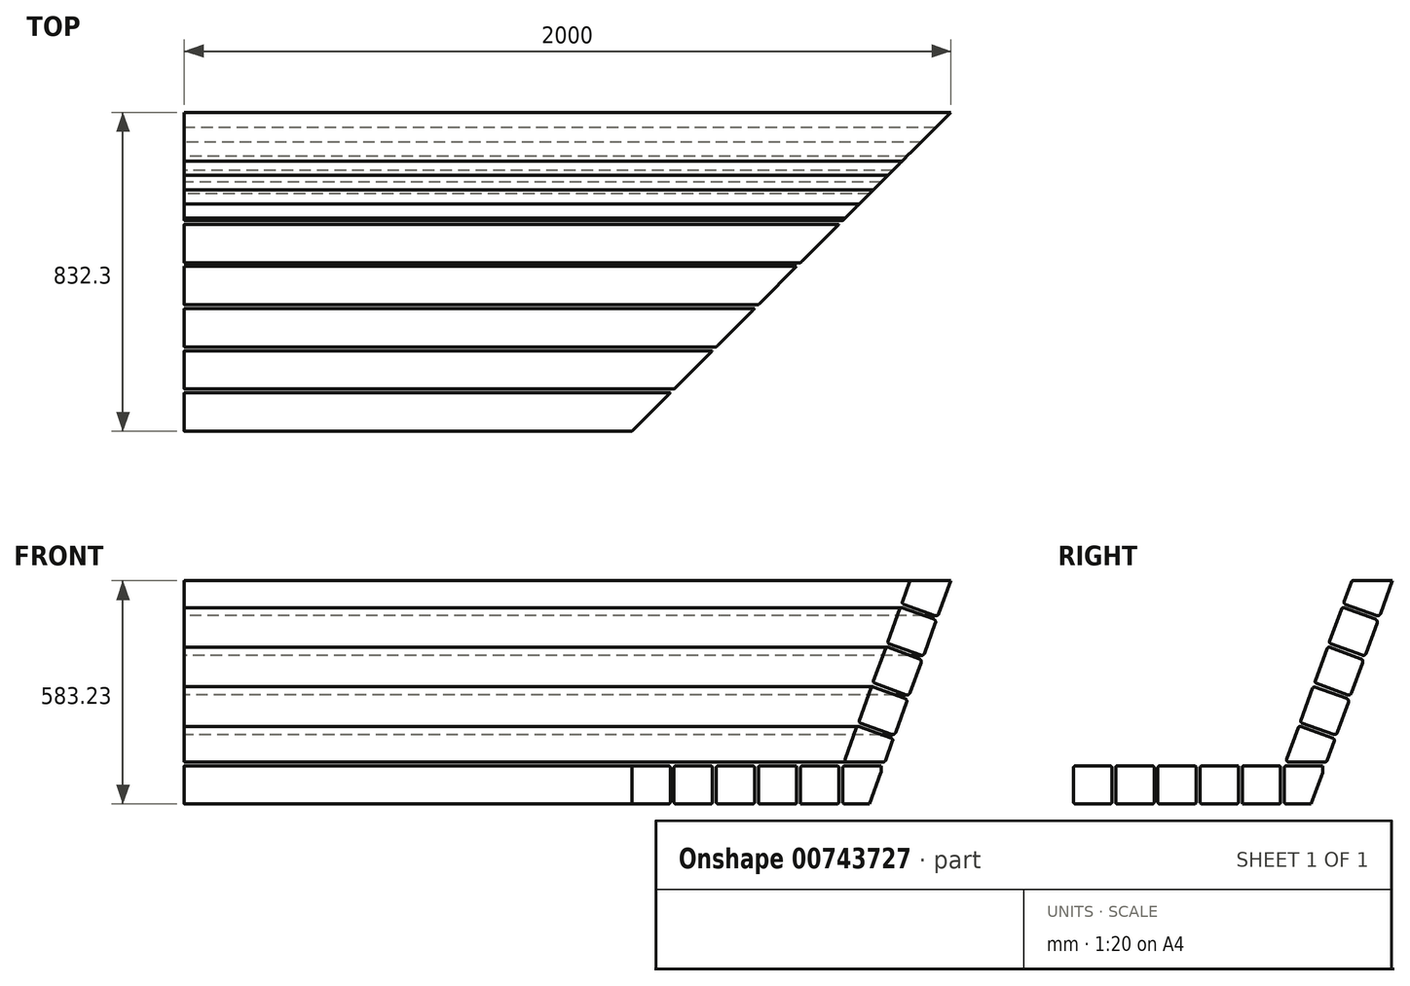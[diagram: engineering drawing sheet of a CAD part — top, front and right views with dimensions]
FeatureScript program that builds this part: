
annotation { "Feature Type Name" : "Feature", "Feature Type Description" : "" }
export const myFeature = defineFeature(function(context is Context, id is Id, definition is map)
    precondition{}
    {
        {
            var Q0;
            Q0=qCreatedBy(makeId("Right.planeOp"),FACE);
            var sketch = newSketch(context, id + "F0", { "sketchPlane" : qUnion([Q0])});
            skLineSegment(sketch, "E0.bottom", {"start": v(0, 0) * mm, "end": v(-95, 0) * mm});
            skLineSegment(sketch, "E0.top", {"start": v(-33.48, -100) * mm, "end": v(-95, -100) * mm});
            skLineSegment(sketch, "E0.left", {"start": v(0, 0) * mm, "end": v(0, -16.75) * mm});
            skLineSegment(sketch, "E0.right", {"start": v(-100, -5) * mm, "end": v(-100, -95) * mm});
            skLineSegment(sketch, "E1.1.0.0", {"start": v(-115, 0) * mm, "end": v(-205, 0) * mm});
            skLineSegment(sketch, "E1.1.0.1", {"start": v(-210, -5) * mm, "end": v(-210, -100) * mm});
            skLineSegment(sketch, "E1.1.0.2", {"start": v(-115, -100) * mm, "end": v(-210, -100) * mm});
            skLineSegment(sketch, "E1.1.0.3", {"start": v(-110, -5) * mm, "end": v(-110, -95) * mm});
            skLineSegment(sketch, "E1.2.0.0", {"start": v(-220, 0) * mm, "end": v(-315, 0) * mm});
            skLineSegment(sketch, "E1.2.0.1", {"start": v(-320, -5) * mm, "end": v(-320, -95) * mm});
            skLineSegment(sketch, "E1.2.0.2", {"start": v(-225, -100) * mm, "end": v(-315, -100) * mm});
            skLineSegment(sketch, "E1.2.0.3", {"start": v(-220, 0) * mm, "end": v(-220, -95) * mm});
            skLineSegment(sketch, "E1.3.0.0", {"start": v(-335, 0) * mm, "end": v(-425, 0) * mm});
            skLineSegment(sketch, "E1.3.0.1", {"start": v(-430, -5) * mm, "end": v(-430, -95) * mm});
            skLineSegment(sketch, "E1.3.0.2", {"start": v(-335, -100) * mm, "end": v(-425, -100) * mm});
            skLineSegment(sketch, "E1.3.0.3", {"start": v(-330, -5) * mm, "end": v(-330, -95) * mm});
            skLineSegment(sketch, "E1.4.0.0", {"start": v(-445, 0) * mm, "end": v(-535, 0) * mm});
            skLineSegment(sketch, "E1.4.0.1", {"start": v(-540, -5) * mm, "end": v(-540, -95) * mm});
            skLineSegment(sketch, "E1.4.0.2", {"start": v(-445, -100) * mm, "end": v(-535, -100) * mm});
            skLineSegment(sketch, "E1.4.0.3", {"start": v(-440, -5) * mm, "end": v(-440, -95) * mm});
            skLineSegment(sketch, "E1.5.0.0", {"start": v(-555, 0) * mm, "end": v(-645, 0) * mm});
            skLineSegment(sketch, "E1.5.0.1", {"start": v(-650, -5) * mm, "end": v(-650, -95) * mm});
            skLineSegment(sketch, "E1.5.0.2", {"start": v(-555, -100) * mm, "end": v(-645, -100) * mm});
            skLineSegment(sketch, "E1.5.0.3", {"start": v(-550, -5) * mm, "end": v(-550, -95) * mm});
            skLineSegment(sketch, "E1.direction1", {"start": v(-100, 0) * mm, "end": v(-210, 0) * mm, "construction": true});
            skLineSegment(sketch, "E2", {"start": v(-93.92, 16.71) * mm, "end": v(-63.87, 99.27) * mm});
            skLineSegment(sketch, "E3", {"start": v(-89.22, 10) * mm, "end": v(6.56, 10) * mm});
            skLineSegment(sketch, "E4", {"start": v(-57.46, 102.26) * mm, "end": v(27.11, 71.48) * mm});
            skLineSegment(sketch, "E5", {"start": v(30.1, 65.07) * mm, "end": v(11.25, 13.29) * mm});
            skPoint(sketch, "E6.orphan", {"position": v(0, -17.63) * mm});
            skLineSegment(sketch, "E7", {"start": v(-54.04, 111.66) * mm, "end": v(27.7, 81.9) * mm});
            skLineSegment(sketch, "E8", {"start": v(37.98, 86.7) * mm, "end": v(66.69, 165.6) * mm});
            skLineSegment(sketch, "E9", {"start": v(61.9, 175.88) * mm, "end": v(-19.84, 205.63) * mm});
            skLineSegment(sketch, "E10.trimOffspring", {"start": v(-57.03, 118.06) * mm, "end": v(-26.25, 202.64) * mm});
            skLineSegment(sketch, "E11", {"start": v(-19.4, 221.43) * mm, "end": v(11.38, 306) * mm});
            skLineSegment(sketch, "E12", {"start": v(182.3, 483.23) * mm, "end": v(150.84, 396.8) * mm});
            skLineSegment(sketch, "E13", {"start": v(-16.42, 215.02) * mm, "end": v(65.31, 185.27) * mm});
            skLineSegment(sketch, "E14", {"start": v(17.78, 309) * mm, "end": v(99.52, 279.24) * mm});
            skLineSegment(sketch, "E15", {"start": v(21.2, 318.39) * mm, "end": v(102.94, 288.64) * mm});
            skLineSegment(sketch, "E16", {"start": v(55.4, 412.36) * mm, "end": v(137.14, 382.6) * mm});
            skLineSegment(sketch, "E17", {"start": v(58.83, 421.75) * mm, "end": v(140.56, 392) * mm});
            skLineSegment(sketch, "E18", {"start": v(182.3, 483.23) * mm, "end": v(79.38, 483.23) * mm});
            skLineSegment(sketch, "E19.trimOffspring", {"start": v(141.93, 372.33) * mm, "end": v(113.22, 293.44) * mm});
            skLineSegment(sketch, "E20.trimOffspring", {"start": v(55.84, 428.16) * mm, "end": v(74.68, 479.94) * mm});
            skLineSegment(sketch, "E21.trimOffspring", {"start": v(18.22, 324.8) * mm, "end": v(49, 409.37) * mm});
            skLineSegment(sketch, "E22.trimOffspring", {"start": v(104.31, 268.96) * mm, "end": v(75.6, 190.07) * mm});
            skLineSegment(sketch, "E23", {"start": v(-0.3, -18.46) * mm, "end": v(-28.78, -96.71) * mm});
            skPoint(sketch, "E24.orphan", {"position": v(0, -100) * mm});
            skArc(sketch, "E25.filletArc", {"start": v(-650, -95) * mm, "mid": v(-648.54, -98.54) * mm, "end": v(-645, -100) * mm});
            skPoint(sketch, "E26.visualSharp", {"position": v(-550, -100) * mm});
            skArc(sketch, "E26.filletArc", {"start": v(-555, -100) * mm, "mid": v(-551.46, -98.54) * mm, "end": v(-550, -95) * mm});
            skPoint(sketch, "E27.visualSharp", {"position": v(-550, 0) * mm});
            skArc(sketch, "E27.filletArc", {"start": v(-550, -5) * mm, "mid": v(-551.46, -1.46) * mm, "end": v(-555, 0) * mm});
            skArc(sketch, "E28.filletArc", {"start": v(-645, 0) * mm, "mid": v(-648.54, -1.46) * mm, "end": v(-650, -5) * mm});
            skPoint(sketch, "E29.visualSharp", {"position": v(-540, 0) * mm});
            skArc(sketch, "E29.filletArc", {"start": v(-535, 0) * mm, "mid": v(-538.54, -1.46) * mm, "end": v(-540, -5) * mm});
            skPoint(sketch, "E30.visualSharp", {"position": v(-540, -100) * mm});
            skArc(sketch, "E30.filletArc", {"start": v(-540, -95) * mm, "mid": v(-538.54, -98.54) * mm, "end": v(-535, -100) * mm});
            skPoint(sketch, "E31.visualSharp", {"position": v(-440, 0) * mm});
            skArc(sketch, "E31.filletArc", {"start": v(-440, -5) * mm, "mid": v(-441.46, -1.46) * mm, "end": v(-445, 0) * mm});
            skPoint(sketch, "E32.visualSharp", {"position": v(-430, 0) * mm});
            skArc(sketch, "E32.filletArc", {"start": v(-425, 0) * mm, "mid": v(-428.54, -1.46) * mm, "end": v(-430, -5) * mm});
            skPoint(sketch, "E33.visualSharp", {"position": v(-440, -100) * mm});
            skArc(sketch, "E33.filletArc", {"start": v(-445, -100) * mm, "mid": v(-441.46, -98.54) * mm, "end": v(-440, -95) * mm});
            skPoint(sketch, "E34.visualSharp", {"position": v(-430, -100) * mm});
            skArc(sketch, "E34.filletArc", {"start": v(-430, -95) * mm, "mid": v(-428.54, -98.54) * mm, "end": v(-425, -100) * mm});
            skPoint(sketch, "E35.visualSharp", {"position": v(-330, 0) * mm});
            skArc(sketch, "E35.filletArc", {"start": v(-330, -5) * mm, "mid": v(-331.46, -1.46) * mm, "end": v(-335, 0) * mm});
            skPoint(sketch, "E36.visualSharp", {"position": v(-330, -100) * mm});
            skArc(sketch, "E36.filletArc", {"start": v(-335, -100) * mm, "mid": v(-331.46, -98.54) * mm, "end": v(-330, -95) * mm});
            skPoint(sketch, "E37.visualSharp", {"position": v(-320, 0) * mm});
            skArc(sketch, "E37.filletArc", {"start": v(-315, 0) * mm, "mid": v(-318.54, -1.46) * mm, "end": v(-320, -5) * mm});
            skPoint(sketch, "E38.visualSharp", {"position": v(-320, -100) * mm});
            skArc(sketch, "E38.filletArc", {"start": v(-320, -95) * mm, "mid": v(-318.54, -98.54) * mm, "end": v(-315, -100) * mm});
            skPoint(sketch, "E39.visualSharp", {"position": v(-220, -100) * mm});
            skArc(sketch, "E39.filletArc", {"start": v(-225, -100) * mm, "mid": v(-221.46, -98.54) * mm, "end": v(-220, -95) * mm});
            skPoint(sketch, "E40.visualSharp", {"position": v(-210, 0) * mm});
            skArc(sketch, "E40.filletArc", {"start": v(-205, 0) * mm, "mid": v(-208.54, -1.46) * mm, "end": v(-210, -5) * mm});
            skPoint(sketch, "E41.visualSharp", {"position": v(-110, -100) * mm});
            skArc(sketch, "E41.filletArc", {"start": v(-115, -100) * mm, "mid": v(-111.46, -98.54) * mm, "end": v(-110, -95) * mm});
            skPoint(sketch, "E42.visualSharp", {"position": v(-110, 0) * mm});
            skArc(sketch, "E42.filletArc", {"start": v(-110, -5) * mm, "mid": v(-111.46, -1.46) * mm, "end": v(-115, 0) * mm});
            skPoint(sketch, "E43.visualSharp", {"position": v(-100, -100) * mm});
            skArc(sketch, "E43.filletArc", {"start": v(-100, -95) * mm, "mid": v(-98.54, -98.54) * mm, "end": v(-95, -100) * mm});
            skPoint(sketch, "E44.visualSharp", {"position": v(-29.98, -100) * mm});
            skPoint(sketch, "E45.visualSharp", {"position": v(-100, 0) * mm});
            skArc(sketch, "E45.filletArc", {"start": v(-95, 0) * mm, "mid": v(-98.54, -1.46) * mm, "end": v(-100, -5) * mm});
            skArc(sketch, "E46.filletArc", {"start": v(-0.3, -18.46) * mm, "mid": v(-0.08, -17.62) * mm, "end": v(0, -16.75) * mm});
            skPoint(sketch, "E47.visualSharp", {"position": v(-96.36, 10) * mm});
            skArc(sketch, "E47.filletArc", {"start": v(-93.92, 16.71) * mm, "mid": v(-93.32, 12.13) * mm, "end": v(-89.22, 10) * mm});
            skPoint(sketch, "E48.visualSharp", {"position": v(10.06, 10) * mm});
            skArc(sketch, "E48.filletArc", {"start": v(6.56, 10) * mm, "mid": v(9.42, 10.9) * mm, "end": v(11.25, 13.29) * mm});
            skPoint(sketch, "E49.visualSharp", {"position": v(-62.16, 103.97) * mm});
            skArc(sketch, "E49.filletArc", {"start": v(-57.46, 102.26) * mm, "mid": v(-61.28, 102.1) * mm, "end": v(-63.87, 99.27) * mm});
            skPoint(sketch, "E50.visualSharp", {"position": v(35.23, 79.16) * mm});
            skArc(sketch, "E50.filletArc", {"start": v(27.7, 81.9) * mm, "mid": v(33.83, 82.18) * mm, "end": v(37.98, 86.7) * mm});
            skPoint(sketch, "E51.visualSharp", {"position": v(-58.74, 113.37) * mm});
            skArc(sketch, "E51.filletArc", {"start": v(-57.03, 118.06) * mm, "mid": v(-56.86, 114.24) * mm, "end": v(-54.04, 111.66) * mm});
            skPoint(sketch, "E52.visualSharp", {"position": v(31.81, 69.77) * mm});
            skArc(sketch, "E52.filletArc", {"start": v(30.1, 65.07) * mm, "mid": v(29.93, 68.9) * mm, "end": v(27.11, 71.48) * mm});
            skPoint(sketch, "E53.visualSharp", {"position": v(69.43, 173.13) * mm});
            skArc(sketch, "E53.filletArc", {"start": v(66.69, 165.6) * mm, "mid": v(66.42, 171.73) * mm, "end": v(61.9, 175.88) * mm});
            skPoint(sketch, "E54.visualSharp", {"position": v(-21.12, 216.73) * mm});
            skArc(sketch, "E54.filletArc", {"start": v(-19.4, 221.43) * mm, "mid": v(-19.24, 217.6) * mm, "end": v(-16.42, 215.02) * mm});
            skPoint(sketch, "E55.visualSharp", {"position": v(-24.54, 207.34) * mm});
            skArc(sketch, "E55.filletArc", {"start": v(-19.84, 205.63) * mm, "mid": v(-23.66, 205.46) * mm, "end": v(-26.25, 202.64) * mm});
            skPoint(sketch, "E56.visualSharp", {"position": v(72.85, 182.53) * mm});
            skArc(sketch, "E56.filletArc", {"start": v(65.31, 185.27) * mm, "mid": v(71.45, 185.54) * mm, "end": v(75.6, 190.07) * mm});
            skPoint(sketch, "E57.visualSharp", {"position": v(107.06, 276.5) * mm});
            skArc(sketch, "E57.filletArc", {"start": v(104.31, 268.96) * mm, "mid": v(104.04, 275.1) * mm, "end": v(99.52, 279.24) * mm});
            skPoint(sketch, "E58.visualSharp", {"position": v(110.48, 285.9) * mm});
            skArc(sketch, "E58.filletArc", {"start": v(102.94, 288.64) * mm, "mid": v(109.07, 288.9) * mm, "end": v(113.22, 293.44) * mm});
            skPoint(sketch, "E59.visualSharp", {"position": v(16.5, 320.1) * mm});
            skArc(sketch, "E59.filletArc", {"start": v(18.22, 324.8) * mm, "mid": v(18.38, 320.97) * mm, "end": v(21.2, 318.39) * mm});
            skPoint(sketch, "E60.visualSharp", {"position": v(13.09, 310.7) * mm});
            skArc(sketch, "E60.filletArc", {"start": v(17.78, 309) * mm, "mid": v(13.96, 308.82) * mm, "end": v(11.38, 306) * mm});
            skPoint(sketch, "E61.visualSharp", {"position": v(144.68, 379.87) * mm});
            skArc(sketch, "E61.filletArc", {"start": v(141.93, 372.33) * mm, "mid": v(141.67, 378.46) * mm, "end": v(137.14, 382.6) * mm});
            skPoint(sketch, "E62.visualSharp", {"position": v(54.13, 423.46) * mm});
            skArc(sketch, "E62.filletArc", {"start": v(55.84, 428.16) * mm, "mid": v(56, 424.34) * mm, "end": v(58.83, 421.75) * mm});
            skPoint(sketch, "E63.visualSharp", {"position": v(182.3, 483.23) * mm});
            skPoint(sketch, "E64.visualSharp", {"position": v(148.1, 389.26) * mm});
            skArc(sketch, "E64.filletArc", {"start": v(140.56, 392) * mm, "mid": v(146.7, 392.27) * mm, "end": v(150.84, 396.8) * mm});
            skPoint(sketch, "E65.visualSharp", {"position": v(50.7, 414.07) * mm});
            skArc(sketch, "E65.filletArc", {"start": v(55.4, 412.36) * mm, "mid": v(51.58, 412.2) * mm, "end": v(49, 409.37) * mm});
            skPoint(sketch, "E66.visualSharp", {"position": v(75.88, 483.23) * mm});
            skArc(sketch, "E66.filletArc", {"start": v(79.38, 483.23) * mm, "mid": v(76.52, 482.33) * mm, "end": v(74.68, 479.94) * mm});
            skLineSegment(sketch, "E67", {"start": v(-28.78, -96.71) * mm, "end": v(-29.98, -100) * mm});
            skLineSegment(sketch, "E68", {"start": v(-29.98, -100) * mm, "end": v(-33.48, -100) * mm});
            skLineSegment(sketch, "E69", {"start": v(-29.38, -98.36) * mm, "end": v(-29.98, -100) * mm});
            skSolve(sketch);
        }
        {
            var Q0;
            Q0=qSketchRegion(id+"F0",true);
            extrude(context, id + "F1", {"entities" : qUnion([Q0]), "depth" : 2000 * mm, "offsetDistance" : 25 * mm});
        }
        {
            var Q0;
            Q0=makeQuery(id+"F1.opExtrude","SWEPT_FACE",FACE,{"disambiguationData":[OSD([sQuery(id+"F0.wireOp",EDGE,"E18")])]});
            var sketch = newSketch(context, id + "F2", { "sketchPlane" : qUnion([Q0])});
            skLineSegment(sketch, "E70.left", {"start": v(2000, 182.3) * mm, "end": v(2000, -650.2) * mm});
            skLineSegment(sketch, "E71", {"start": v(1167.5, -650.2) * mm, "end": v(2000, -650.2) * mm});
            skLineSegment(sketch, "E72", {"start": v(2000, 182.3) * mm, "end": v(1167.5, -650.2) * mm});
            skSolve(sketch);
        }
        {
            var Q0;
            {var subQ1=sQuery(id+"F2.wireOp",EDGE,"E70.left");var subQ2=sQuery(id+"F0.wireOp",EDGE,"E18");var subQ4=makeQuery(id+"F1.opExtrude","SWEPT_EDGE",EDGE,{"disambiguationData":[OSD([subQ2,sQuery(id+"F0.wireOp",EDGE,"E66.filletArc")])]});var subQ5=makeQuery(id+"F2.imprint","INTERSECT",VERTEX,{"derivedFrom":[subQ4,subQ1]});Q0=makeQuery(id+"F2.imprint","IMPRINT",FACE,{"disambiguationData":[TD([[makeQuery(id+"F2.imprint","IMPRINT",EDGE,{"disambiguationData":[TD([[subQ5,1.0]])],"derivedFrom":subQ1}),-1.0]])]});}
            var Q1;
            {var subQ3=sQuery(id+"F2.wireOp",EDGE,"E71");Q1=makeQuery(id+"F2.imprint","IMPRINT",FACE,{"disambiguationData":[TD([[makeQuery(id+"F2.imprint","IMPRINT",EDGE,{"derivedFrom":subQ3}),1.0]])]});}
            extrude(context, id + "F3", {"entities" : qUnion([Q0, Q1]), "operationType" : NewBodyOperationType.REMOVE, "endBound" : BoundingType.THROUGH_ALL, "oppositeDirection" : true, "depth" : 25 * mm, "offsetDistance" : 25 * mm});
        }
    });
